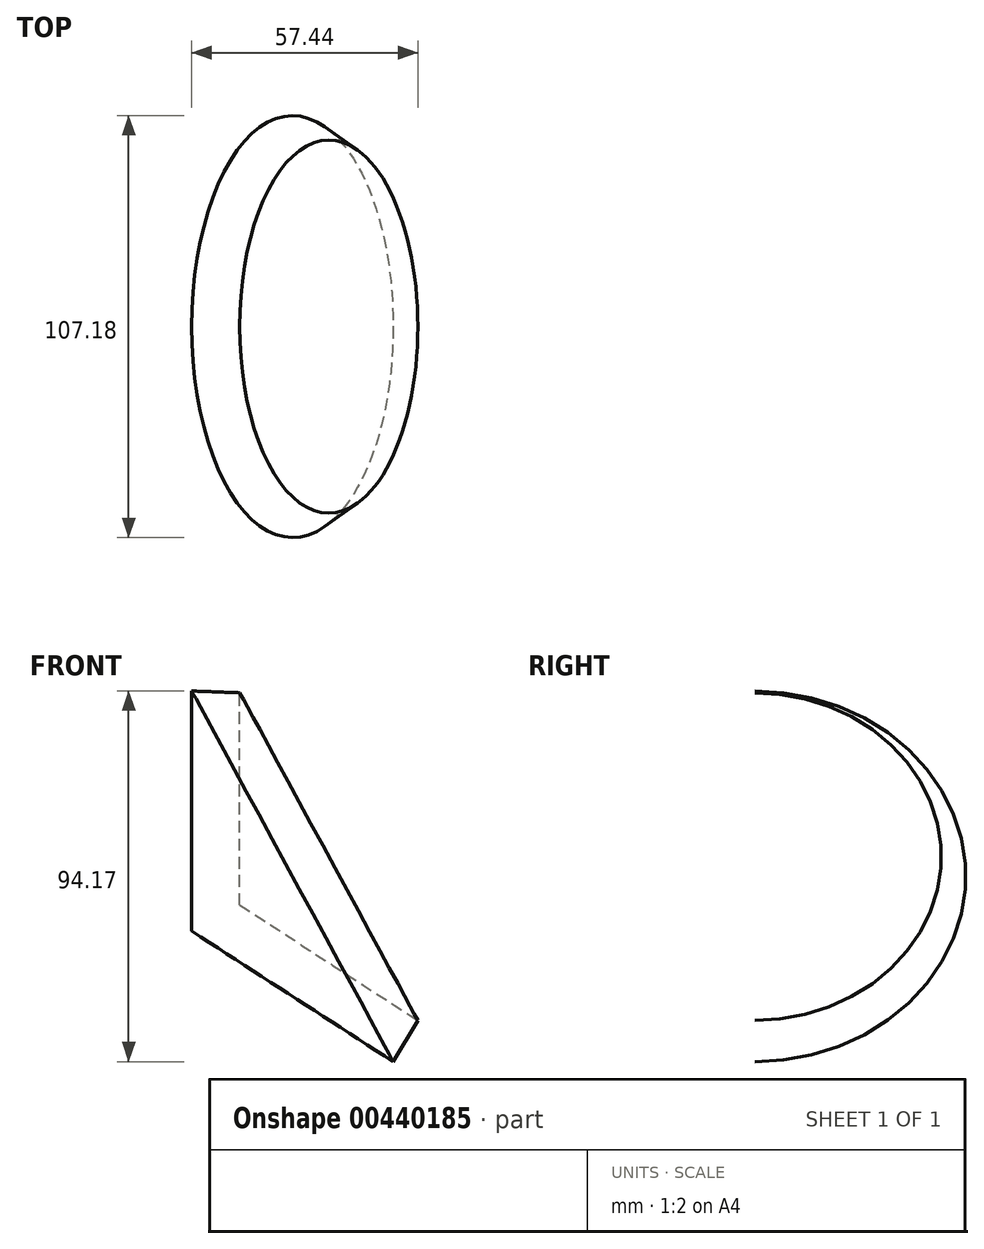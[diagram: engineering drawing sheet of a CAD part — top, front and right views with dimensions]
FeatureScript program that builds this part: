
annotation { "Feature Type Name" : "Feature", "Feature Type Description" : "" }
export const myFeature = defineFeature(function(context is Context, id is Id, definition is map)
    precondition{}
    {
        {
            var Q0;
            Q0=qCreatedBy(makeId("Front.planeOp"),FACE);
            var sketch = newSketch(context, id + "F0", { "sketchPlane" : qUnion([Q0])});
            skLineSegment(sketch, "E0", {"start": v(-29.19, 49.88) * mm, "end": v(-29.19, -11.1) * mm});
            skLineSegment(sketch, "E1", {"start": v(-16.99, 49.44) * mm, "end": v(-29.19, 49.88) * mm});
            skLineSegment(sketch, "E2", {"start": v(-16.99, 49.44) * mm, "end": v(-16.99, -4.48) * mm});
            skLineSegment(sketch, "E3", {"start": v(-29.19, -11.1) * mm, "end": v(-16.99, -4.48) * mm});
            skSolve(sketch);
        }
        {
            var Q0;
            Q0=makeQuery(id+"F0.imprint","IMPRINT",FACE,{"disambiguationData":[TD([[makeQuery(id+"F0.imprint","IMPRINT",EDGE,{"derivedFrom":sQuery(id+"F0.wireOp",EDGE,"E0")}),1.0]])]});
            var Q1;
            Q1=sQuery(id+"F0.wireOp",EDGE,"E3");
            revolve(context, id + "F1", {"entities" : qUnion([Q0]), "axis" : qUnion([Q1]), "revolveType" : RevolveType.FULL});
        }
    });
